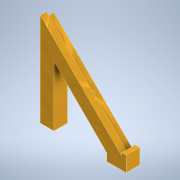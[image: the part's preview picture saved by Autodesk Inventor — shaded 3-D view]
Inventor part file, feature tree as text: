
AUTODESK INVENTOR PART (.ipt)
format: ipt  version: 2022.2 (Build 262287010, 287A)  size: 166,912 bytes
history: native  units: in
note: dims shown in document units (in); Inventor stores cm internally (conversion verified against a paired STEP export)
features: sketch x7, extrude x6, other x1, plane x1, mirror x1
ambient origin geometry x8: Origin, YZ Plane, XZ Plane, XY Plane, X Axis, Y Axis, Z Axis, Center Point
bodies: Body1 (feature_tree)
feature tree (16):
  other  "Sólido1"
  extrude  "Extrusión1"  TaperAngle=45.0deg  [1 undecoded]
  extrude  "Extrusión2"  Depth=0.1181in
  extrude  "Extrusión3"  Depth=0.3543in TaperAngle=0.0deg
  extrude  "Extrusión4"  Depth=1.378in
  extrude  "Extrusión5"  Depth=0.5906in TaperAngle=0.0deg
  extrude  "Extrusión6"  Depth=0.1969in TaperAngle=0.0deg
  plane  "Plano de trabajo1"
  mirror  "Simetría2"
  sketch  "Boceto8"  dims[d27=0.1969in d28=0.0in d29=-0.7874in d30=7.874in d15=0.0197in d16=0.0344in]
  sketch  "Boceto1"  dims[d0=2.126in d2=45.0deg]
  sketch  "Boceto2"  dims[d3=0.1969in d4=0.0in d9=0.1181in]
  sketch  "Boceto4"  dims[d10=0.1969in d11=0.3543in d12=0.0in]
  sketch  "Boceto5"  dims[d17=0.1575in d18=0.0in d19=1.378in]
  sketch  "Boceto6"  dims[d20=135.0deg d21=0.5906in d22=0.0in]
  sketch  "Boceto7"  dims[d24=45.0deg d25=0.1969in d26=0.0in]
note: 1 required parameter value undecoded (feature->parameter linkage not recoverable at this tier; creation-order binding heuristic only, values carry confidence <= 0.55)
